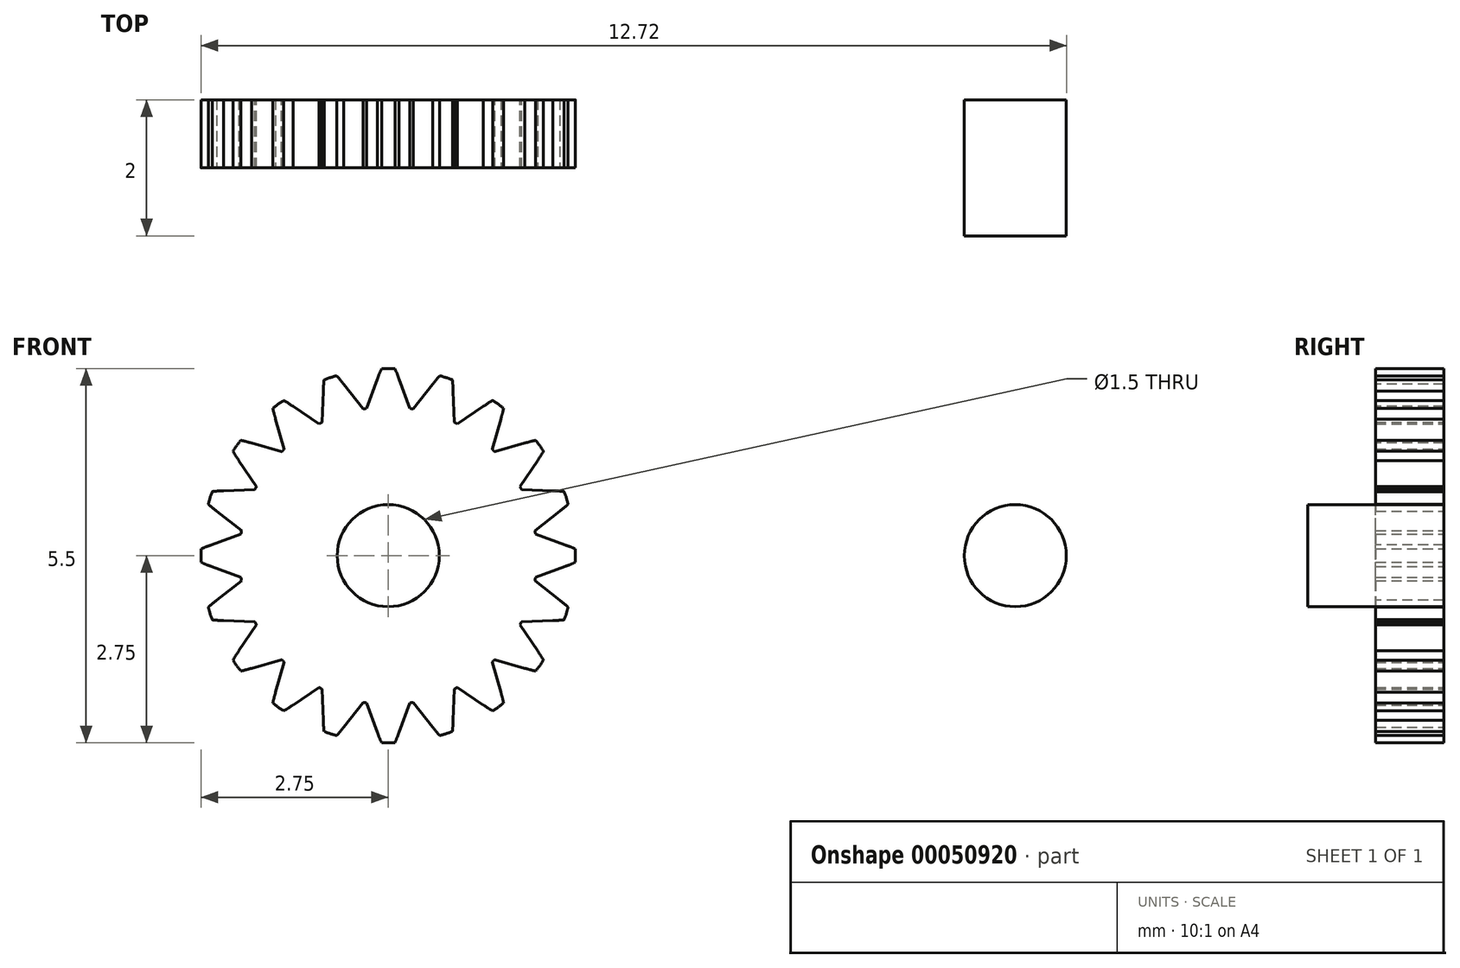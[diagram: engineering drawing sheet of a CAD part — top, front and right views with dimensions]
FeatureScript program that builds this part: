
annotation { "Feature Type Name" : "Feature", "Feature Type Description" : "" }
export const myFeature = defineFeature(function(context is Context, id is Id, definition is map)
    precondition{}
    {
        {
            assignVariable(context, id + "F0", {"name" : "N", "anyValue" : 20});
        }
        {
            var Q0;
            Q0=qCreatedBy(makeId("Front.planeOp"),FACE);
            var sketch = newSketch(context, id + "F1", { "sketchPlane" : qUnion([Q0])});
            skArc(sketch, "E0", {"start": v(-0.32, 2.16) * mm, "mid": v(0, -2.19) * mm, "end": v(0.32, 2.16) * mm});
            skLineSegment(sketch, "E1", {"start": v(0, 0) * mm, "end": v(0, 3.03) * mm, "construction": true});
            skArc(sketch, "E2", {"start": v(-0.2, 2.5) * mm, "mid": v(0, -2.5) * mm, "end": v(0.2, 2.5) * mm, "construction": true});
            skCircle(sketch, "E3", {"center": v(0, 0) * mm, "radius": 2.75 * mm, "construction": true});
            skPoint(sketch, "E4", {"position": v(-0.2, 2.5) * mm});
            skPoint(sketch, "E5", {"position": v(0.2, 2.5) * mm});
            skPoint(sketch, "E6", {"position": v(0, 2.19) * mm});
            skLineSegment(sketch, "E7", {"start": v(-0.2, 2.5) * mm, "end": v(-0.2, 2.5) * mm});
            skLineSegment(sketch, "E8", {"start": v(0.2, 2.5) * mm, "end": v(-0.2, 2.5) * mm, "construction": true});
            skLineSegment(sketch, "E9", {"start": v(-0.2, 2.5) * mm, "end": v(-0.2, 2.74) * mm, "construction": true});
            skLineSegment(sketch, "E10", {"start": v(-0.2, 2.5) * mm, "end": v(-0.56, 2.5) * mm, "construction": true});
            skLineSegment(sketch, "E11", {"start": v(-0.2, 2.5) * mm, "end": v(-0.74, 2.7) * mm, "construction": true});
            skLineSegment(sketch, "E12", {"start": v(-0.32, 2.16) * mm, "end": v(-0.16, 2.6) * mm});
            skPoint(sketch, "E13", {"position": v(-0.1, 2.75) * mm});
            skPoint(sketch, "E14", {"position": v(-0.16, 2.6) * mm});
            skFitSpline(sketch, "E15", {"points": [v(-0.16, 2.6) * mm, v(-0.13, 2.68) * mm, v(-0.1, 2.75) * mm], "startDerivative": vector(0.06, 0.16) * mm, "endDerivative": vector(0.07, 0.15) * mm});
            skLineSegment(sketch, "E16", {"start": v(-0.1, 2.75) * mm, "end": v(-0.16, 2.6) * mm, "construction": true});
            skLineSegment(sketch, "E17", {"start": v(-0.1, 2.75) * mm, "end": v(-0.1, 2.75) * mm, "construction": true});
            skFitSpline(sketch, "E18.MirrorCS", {"points": [v(0.16, 2.6) * mm, v(0.13, 2.68) * mm, v(0.1, 2.75) * mm], "startDerivative": vector(-0.06, 0.16) * mm, "endDerivative": vector(-0.07, 0.15) * mm});
            skLineSegment(sketch, "E19.MirrorCS", {"start": v(0.32, 2.16) * mm, "end": v(0.16, 2.6) * mm});
            skArc(sketch, "E20", {"start": v(0.1, 2.75) * mm, "mid": v(0, 2.75) * mm, "end": v(-0.1, 2.75) * mm});
            skPoint(sketch, "E21", {"position": v(0, 2.75) * mm});
            skCircle(sketch, "E22", {"center": v(0, 0) * mm, "radius": 0.75 * mm});
            skSolve(sketch);
        }
        {
            var Q0;
            Q0=makeQuery(id+"F1.imprint","IMPRINT",FACE,{"disambiguationData":[TD([[makeQuery(id+"F1.imprint","IMPRINT",EDGE,{"derivedFrom":sQuery(id+"F1.wireOp",EDGE,"aaed8282-5219-493e-8fc1-45bb34d14112")}),-1.0]])]});
            var Q1;
            {var subQ0=sQuery(id+"F1.wireOp",EDGE,"E0");Q1=makeQuery(id+"F1.imprint","IMPRINT",FACE,{"disambiguationData":[TD([[makeQuery(id+"F1.imprint","IMPRINT",EDGE,{"derivedFrom":subQ0}),1.0]])]});}
            extrude(context, id + "F2", {"entities" : qUnion([Q0, Q1]), "depth" : 1 * mm});
        }
        {
            var Q0;
            Q0=makeQuery(id+"F2.opExtrude","SWEPT_BODY",BODY,{"disambiguationData":[OSD([sQuery(id+"F1.wireOp",EDGE,"E0"),sQuery(id+"F1.wireOp",EDGE,"aaed8282-5219-493e-8fc1-45bb34d14112"),sQuery(id+"F1.wireOp",EDGE,"53940128-b436-48a2-a5d0-82388a849f59"),sQuery(id+"F1.wireOp",EDGE,"d1044b8d-7fd9-448b-a64e-651761b72f81.filletArc"),sQuery(id+"F1.wireOp",EDGE,"9b7c7921-a636-4215-afc9-d0644dfa7fa70.MirrorCS"),sQuery(id+"F1.wireOp",EDGE,"144ef5e2-5575-4e56-b415-ed7f0af654610.MirrorCS"),sQuery(id+"F1.wireOp",EDGE,"098adab9-8a0a-44c9-b43f-ca0d8f639d210.MirrorCS"),sQuery(id+"F1.wireOp",EDGE,"77ef0924-f486-4a39-82b1-a400a53a18c2")])]});
            var Q1;
            Q1=sQuery(id+"F1.wireOp",EDGE,"E2");
            circularPattern(context, id + "F3", {"operationType" : NewBodyOperationType.ADD, "entities" : qUnion([Q0]), "axis" : qUnion([Q1]), "angle" : (360 / getVariable(context, 'N')) * degree, "instanceCount" : getVariable(context, 'N')});
        }
        {
            var Q0;
            Q0=qCreatedBy(makeId("Front.planeOp"),FACE);
            var sketch = newSketch(context, id + "F4", { "sketchPlane" : qUnion([Q0])});
            skCircle(sketch, "E23", {"center": v(9.22, 0) * mm, "radius": 0.75 * mm});
            skSolve(sketch);
        }
        {
            var Q0;
            Q0=makeQuery(id+"F4.imprint","IMPRINT",FACE,{"disambiguationData":[TD([[makeQuery(id+"F4.imprint","IMPRINT",EDGE,{"derivedFrom":sQuery(id+"F4.wireOp",EDGE,"E23")}),1.0]])]});
            extrude(context, id + "F5", {"entities" : qUnion([Q0]), "depth" : 2 * mm});
        }
    });
